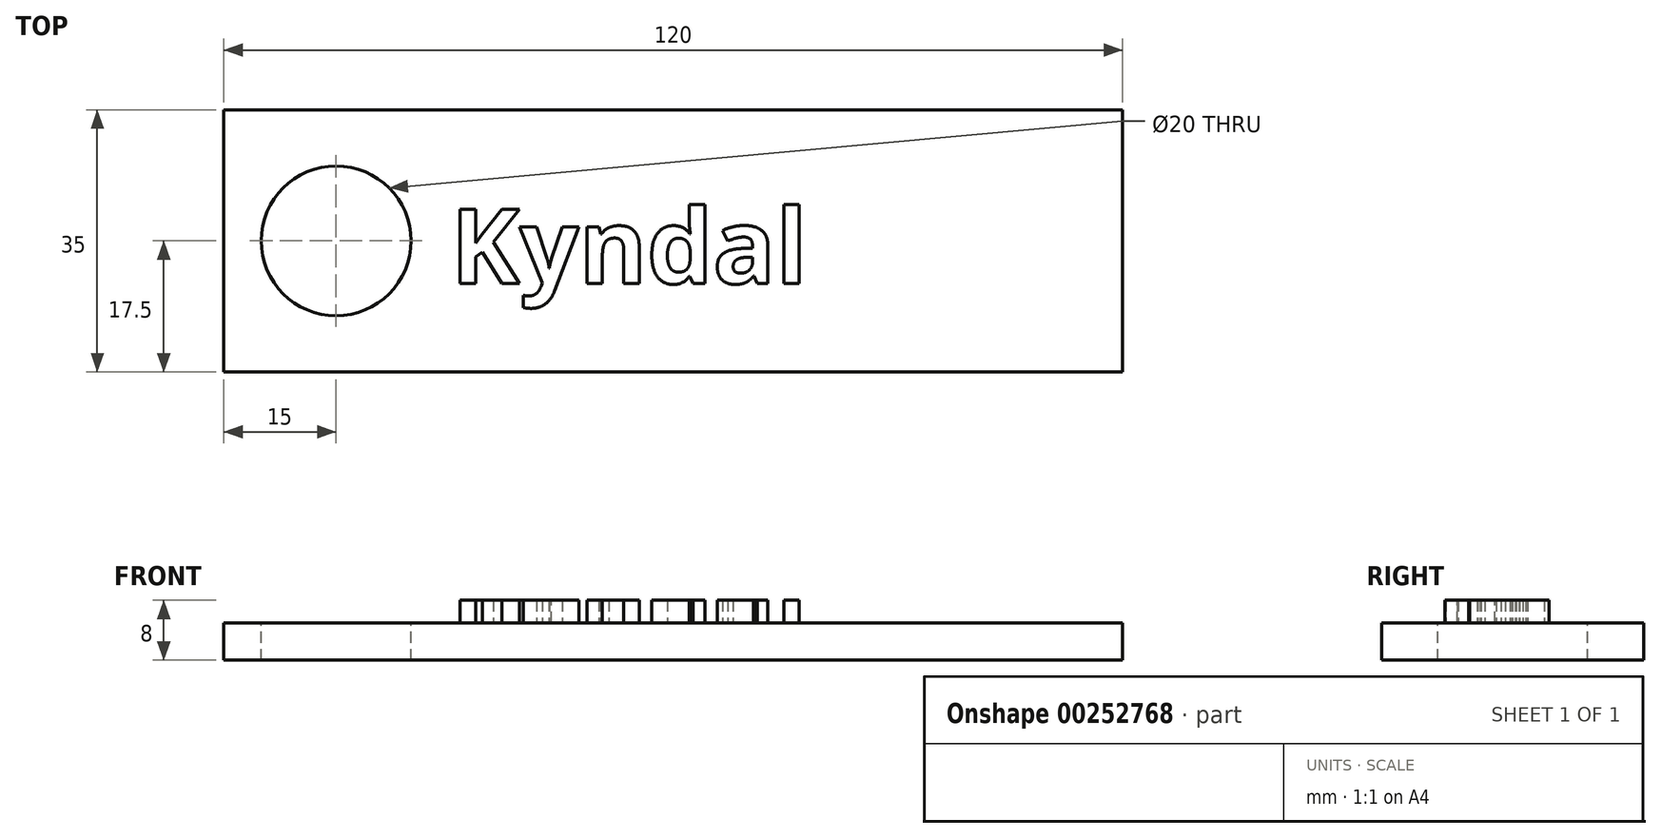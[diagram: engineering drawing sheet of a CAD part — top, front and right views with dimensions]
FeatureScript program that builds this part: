
annotation { "Feature Type Name" : "Feature", "Feature Type Description" : "" }
export const myFeature = defineFeature(function(context is Context, id is Id, definition is map)
    precondition{}
    {
        {
            var Q0;
            Q0=qCreatedBy(makeId("Top.planeOp"),FACE);
            var sketch = newSketch(context, id + "F0", { "sketchPlane" : qUnion([Q0])});
            skLineSegment(sketch, "E0.bottom", {"start": v(-60, -17.5) * mm, "end": v(60, -17.5) * mm});
            skLineSegment(sketch, "E0.top", {"start": v(-60, 17.5) * mm, "end": v(60, 17.5) * mm});
            skLineSegment(sketch, "E0.left", {"start": v(-60, -17.5) * mm, "end": v(-60, 17.5) * mm});
            skLineSegment(sketch, "E0.right", {"start": v(60, -17.5) * mm, "end": v(60, 17.5) * mm});
            skPoint(sketch, "E0.middle", {"position": v(0, 0) * mm});
            skCircle(sketch, "E1", {"center": v(-45, 0) * mm, "radius": 10 * mm});
            skSolve(sketch);
        }
        {
            var Q0;
            Q0 = qSketchRegion(id + "F0", true);
            extrude(context, id + "F1", {"entities" : qUnion([Q0]), "oppositeDirection" : true, "depth" : 5 * mm});
        }
        {
            var Q0;
            Q0=makeQuery(id+"F1.opExtrude","CAP_FACE",FACE,{"disambiguationData":[OSD([sQuery(id+"F0.wireOp",EDGE,"E0.bottom"),sQuery(id+"F0.wireOp",EDGE,"E0.top"),sQuery(id+"F0.wireOp",EDGE,"E0.left"),sQuery(id+"F0.wireOp",EDGE,"E0.right"),sQuery(id+"F0.wireOp",EDGE,"E1")])],"isStart":true});
            var sketch = newSketch(context, id + "F2", { "sketchPlane" : qUnion([Q0])});
            skText(sketch, "E2", { "text": "Kyndal", "fontName": "OpenSans-Bold.ttf"});
            const initialGuessF2  = {"E2": [-0.02973, -0.00569, 1, 0, 0.01]};
            skSetInitialGuess(sketch, initialGuessF2);
            skSolve(sketch);
        }
        {
            var Q0;
            Q0=makeQuery(id+"F2.imprint","IMPRINT",FACE,{"disambiguationData":[TD([[makeQuery(id+"F2.imprint","IMPRINT",EDGE,{"derivedFrom":sQuery(id+"F2.wireOp",EDGE,"E2.sketch_text.stroke-0")}),1.0]])]});
            var sketch = newSketch(context, id + "F3", { "sketchPlane" : qUnion([Q0])});
            skLineSegment(sketch, "E3", {"start": v(42.08, 27.68) * mm, "end": v(42.08, -29.39) * mm, "construction": true});
            skFitSpline(sketch, "E4", {"points": [v(42.08, 1.87) * mm, v(38.04, 4.49) * mm, v(33.6, 3.48) * mm, v(35.62, -3.78) * mm, v(42.08, -9.02) * mm], "startDerivative": vector(-16.12, 14.87) * mm, "endDerivative": vector(24.06, -14.39) * mm});
            skFitSpline(sketch, "E5.MirrorCS", {"points": [v(42.08, 1.87) * mm, v(46.1, 4.49) * mm, v(50.55, 3.48) * mm, v(48.53, -3.78) * mm, v(42.08, -9.02) * mm], "startDerivative": vector(16.12, 14.87) * mm, "endDerivative": vector(-24.06, -14.39) * mm});
            skSolve(sketch);
        }
        {
            var Q0;
            Q0=makeQuery(id+"F2.imprint","IMPRINT",FACE,{"disambiguationData":[TD([[makeQuery(id+"F2.imprint","IMPRINT",EDGE,{"derivedFrom":sQuery(id+"F2.wireOp",EDGE,"E2.sketch_text.stroke-0")}),-1.0]])]});
            var Q1;
            Q1=makeQuery(id+"F2.imprint","IMPRINT",FACE,{"disambiguationData":[TD([[makeQuery(id+"F2.imprint","IMPRINT",EDGE,{"derivedFrom":sQuery(id+"F2.wireOp",EDGE,"E2.sketch_text.stroke-13")}),-1.0]])]});
            var Q2;
            Q2=makeQuery(id+"F2.imprint","IMPRINT",FACE,{"disambiguationData":[TD([[makeQuery(id+"F2.imprint","IMPRINT",EDGE,{"derivedFrom":sQuery(id+"F2.wireOp",EDGE,"E2.sketch_text.stroke-30")}),-1.0]])]});
            var Q3;
            Q3=makeQuery(id+"F2.imprint","IMPRINT",FACE,{"disambiguationData":[TD([[makeQuery(id+"F2.imprint","IMPRINT",EDGE,{"derivedFrom":sQuery(id+"F2.wireOp",EDGE,"E2.sketch_text.stroke-47")}),-1.0]])]});
            var Q4;
            Q4=makeQuery(id+"F2.imprint","IMPRINT",FACE,{"disambiguationData":[TD([[makeQuery(id+"F2.imprint","IMPRINT",EDGE,{"derivedFrom":sQuery(id+"F2.wireOp",EDGE,"E2.sketch_text.stroke-70")}),-1.0]])]});
            var Q5;
            Q5=makeQuery(id+"F2.imprint","IMPRINT",FACE,{"disambiguationData":[TD([[makeQuery(id+"F2.imprint","IMPRINT",EDGE,{"derivedFrom":sQuery(id+"F2.wireOp",EDGE,"E2.sketch_text.stroke-95")}),-1.0]])]});
            extrude(context, id + "F4", {"entities" : qUnion([Q0, Q1, Q2, Q3, Q4, Q5]), "operationType" : NewBodyOperationType.ADD, "depth" : 3 * mm});
        }
        {
            var Q0;
            Q0=sQuery(id+"F3.wireOp",EDGE,"E5.MirrorCS");
            var Q1;
            Q1=sQuery(id+"F3.wireOp",EDGE,"E4");
            extrude(context, id + "F5", {"bodyType" : ToolBodyType.SURFACE, "surfaceEntities" : qUnion([Q0, Q1]), "depth" : 3 * mm});
        }
    });
